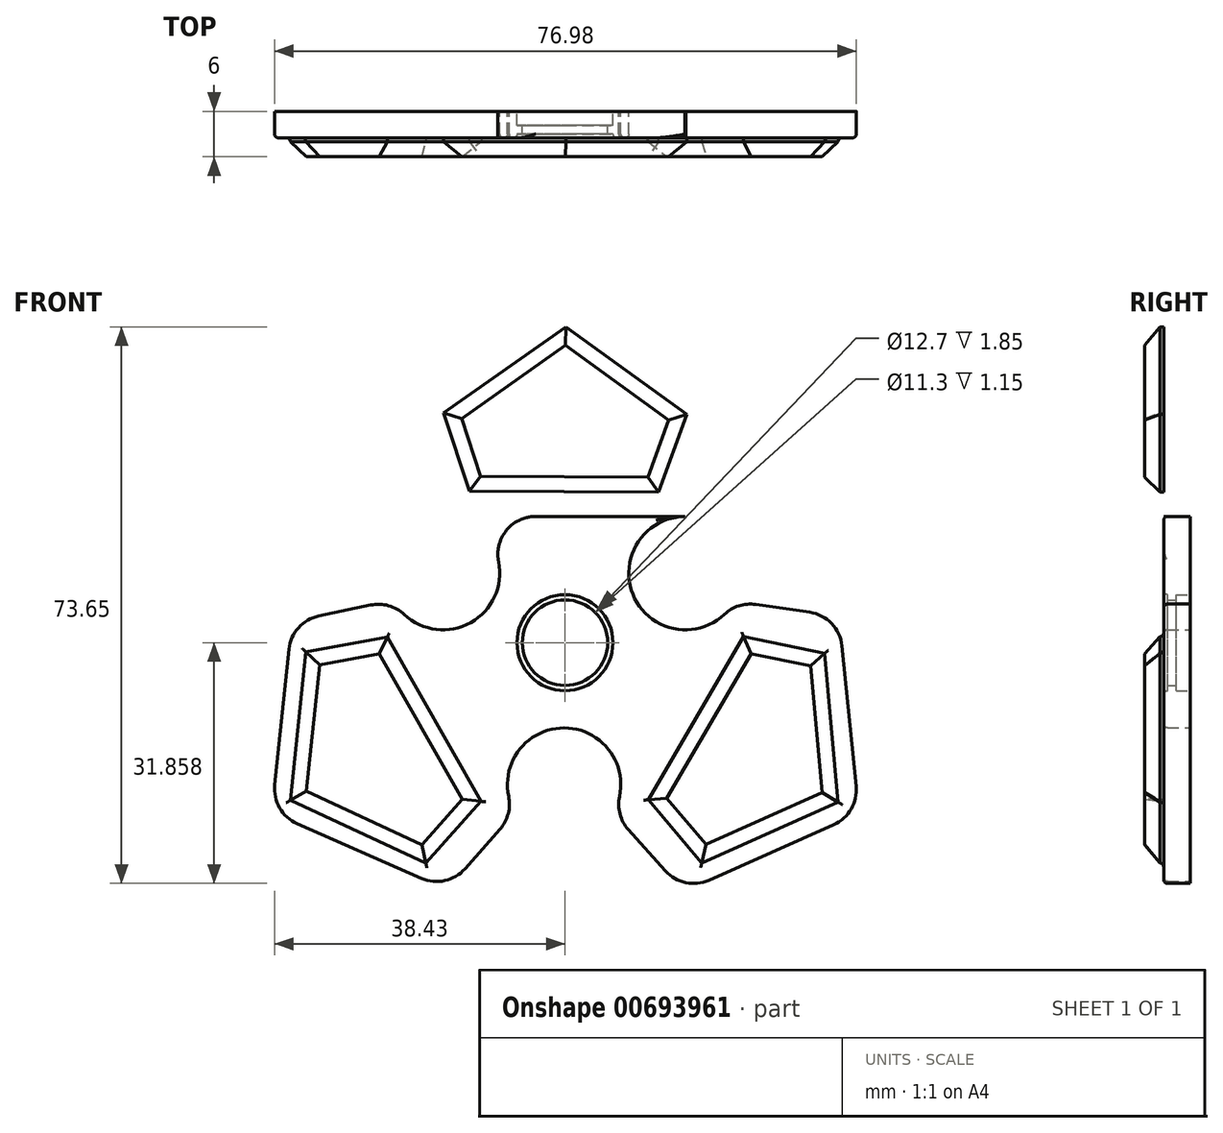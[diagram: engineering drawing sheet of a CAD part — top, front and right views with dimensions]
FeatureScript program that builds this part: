
annotation { "Feature Type Name" : "Feature", "Feature Type Description" : "" }
export const myFeature = defineFeature(function(context is Context, id is Id, definition is map)
    precondition{}
    {
        {
            var Q0;
            Q0=qCreatedBy(makeId("Front.planeOp"),FACE);
            var sketch = newSketch(context, id + "F0", { "sketchPlane" : qUnion([Q0])});
            skPoint(sketch, "E0.center", {"position": v(-0.03, -0.92) * mm});
            skLineSegment(sketch, "E1.0", {"start": v(15.99, 15.77) * mm, "end": v(-16.16, 15.77) * mm});
            skLineSegment(sketch, "E1.1", {"start": v(-16.16, 15.77) * mm, "end": v(-20.52, 29.1) * mm});
            skLineSegment(sketch, "E1.2", {"start": v(-20.52, 29.1) * mm, "end": v(0, 44.01) * mm});
            skLineSegment(sketch, "E1.3", {"start": v(0, 44.01) * mm, "end": v(20.51, 29.1) * mm});
            skLineSegment(sketch, "E1.4", {"start": v(20.51, 29.1) * mm, "end": v(15.99, 15.77) * mm});
            skPoint(sketch, "E1.0.midPoint", {"position": v(-0.09, 15.77) * mm});
            skLineSegment(sketch, "E2.1.0", {"start": v(22.42, 4.54) * mm, "end": v(36.23, 2.53) * mm});
            skLineSegment(sketch, "E2.1.2", {"start": v(36.23, 2.53) * mm, "end": v(38.86, -23.51) * mm});
            skLineSegment(sketch, "E2.1.3", {"start": v(6.36, -23.44) * mm, "end": v(22.42, 4.54) * mm});
            skLineSegment(sketch, "E2.1.4", {"start": v(15.7, -33.83) * mm, "end": v(6.36, -23.44) * mm});
            skLineSegment(sketch, "E2.1.5", {"start": v(38.86, -23.51) * mm, "end": v(15.7, -33.83) * mm});
            skLineSegment(sketch, "E2.2.0", {"start": v(-6.68, -23.39) * mm, "end": v(-15.67, -33.57) * mm});
            skLineSegment(sketch, "E2.2.2", {"start": v(-15.67, -33.57) * mm, "end": v(-38.81, -23.39) * mm});
            skLineSegment(sketch, "E2.2.3", {"start": v(-22.75, 4.69) * mm, "end": v(-6.68, -23.39) * mm});
            skLineSegment(sketch, "E2.2.4", {"start": v(-36.16, 1.84) * mm, "end": v(-22.75, 4.69) * mm});
            skLineSegment(sketch, "E2.2.5", {"start": v(-38.81, -23.39) * mm, "end": v(-36.16, 1.84) * mm});
            skPoint(sketch, "E2.center", {"position": v(0, -0.83) * mm});
            skArc(sketch, "E3", {"start": v(15.99, 15.77) * mm, "mid": v(9.4, 4.55) * mm, "end": v(22.42, 4.54) * mm});
            skArc(sketch, "E4", {"start": v(-22.75, 4.69) * mm, "mid": v(-9.71, 4.44) * mm, "end": v(-16.16, 15.77) * mm});
            skArc(sketch, "E5", {"start": v(6.36, -23.44) * mm, "mid": v(-0.11, -12.2) * mm, "end": v(-6.68, -23.39) * mm});
            skCircle(sketch, "E6", {"center": v(-0.03, -0.92) * mm, "radius": 6.35 * mm});
            skCircle(sketch, "E7", {"center": v(-0.03, -0.92) * mm, "radius": 5.65 * mm});
            skSolve(sketch);
        }
        {
            var Q0;
            Q0=makeQuery(id+"F0.imprint","IMPRINT",FACE,{"disambiguationData":[TD([[makeQuery(id+"F0.imprint","IMPRINT",EDGE,{"derivedFrom":sQuery(id+"F0.wireOp",EDGE,"E2.1.0")}),-1.0]])]});
            var Q1;
            {var subQ0=sQuery(id+"F0.wireOp",EDGE,"E1.0");Q1=makeQuery(id+"F0.imprint","IMPRINT",FACE,{"disambiguationData":[TD([[makeQuery(id+"F0.imprint","IMPRINT",EDGE,{"derivedFrom":subQ0}),-1.0]])]});}
            var Q2;
            {var subQ5=sQuery(id+"F0.wireOp",EDGE,"E1.0");Q2=makeQuery(id+"F0.imprint","IMPRINT",FACE,{"disambiguationData":[TD([[makeQuery(id+"F0.imprint","IMPRINT",EDGE,{"derivedFrom":subQ5}),1.0]])]});}
            var Q3;
            {var subQ2=sQuery(id+"F0.wireOp",EDGE,"E2.2.0");Q3=makeQuery(id+"F0.imprint","IMPRINT",FACE,{"disambiguationData":[TD([[makeQuery(id+"F0.imprint","IMPRINT",EDGE,{"derivedFrom":subQ2}),-1.0]])]});}
            extrude(context, id + "F1", {"entities" : qUnion([Q0, Q1, Q2, Q3]), "depth" : 3.5 * mm, "offsetDistance" : 25 * mm});
        }
        {
            var Q0;
            Q0=makeQuery(id+"F1.opExtrude","CAP_FACE",FACE,{"disambiguationData":[OSD([sQuery(id+"F0.wireOp",EDGE,"E1.1"),sQuery(id+"F0.wireOp",EDGE,"E1.2"),sQuery(id+"F0.wireOp",EDGE,"E1.3"),sQuery(id+"F0.wireOp",EDGE,"E1.4"),sQuery(id+"F0.wireOp",EDGE,"E2.1.0"),sQuery(id+"F0.wireOp",EDGE,"E2.1.2"),sQuery(id+"F0.wireOp",EDGE,"E2.1.4"),sQuery(id+"F0.wireOp",EDGE,"E2.1.5"),sQuery(id+"F0.wireOp",EDGE,"E2.2.0"),sQuery(id+"F0.wireOp",EDGE,"E2.2.2"),sQuery(id+"F0.wireOp",EDGE,"E2.2.4"),sQuery(id+"F0.wireOp",EDGE,"E2.2.5"),sQuery(id+"F0.wireOp",EDGE,"E3"),sQuery(id+"F0.wireOp",EDGE,"E4"),sQuery(id+"F0.wireOp",EDGE,"E5")])],"isStart":false});
            var sketch = newSketch(context, id + "F2", { "sketchPlane" : qUnion([Q0])});
            skLineSegment(sketch, "E8.0", {"start": v(12.36, 18.97) * mm, "end": v(-12.64, 19.1) * mm});
            skLineSegment(sketch, "E8.1", {"start": v(-12.64, 19.1) * mm, "end": v(-16.08, 29.5) * mm});
            skLineSegment(sketch, "E8.2", {"start": v(-16.08, 29.5) * mm, "end": v(0.08, 40.87) * mm});
            skLineSegment(sketch, "E8.3", {"start": v(0.08, 40.87) * mm, "end": v(16.07, 29.27) * mm});
            skLineSegment(sketch, "E8.4", {"start": v(16.07, 29.27) * mm, "end": v(12.36, 18.97) * mm});
            skLineSegment(sketch, "E9.1.0", {"start": v(-23.54, -0.2) * mm, "end": v(-11.15, -21.92) * mm});
            skLineSegment(sketch, "E9.1.1", {"start": v(-34.32, -2.14) * mm, "end": v(-23.54, -0.2) * mm});
            skLineSegment(sketch, "E9.1.2", {"start": v(-36.37, -21.8) * mm, "end": v(-34.32, -2.14) * mm});
            skLineSegment(sketch, "E9.1.3", {"start": v(-18.44, -30.1) * mm, "end": v(-36.37, -21.8) * mm});
            skLineSegment(sketch, "E9.1.4", {"start": v(-11.15, -21.92) * mm, "end": v(-18.44, -30.1) * mm});
            skLineSegment(sketch, "E9.2.0", {"start": v(11.01, -21.7) * mm, "end": v(23.62, -0.12) * mm});
            skLineSegment(sketch, "E9.2.1", {"start": v(18.08, -30.08) * mm, "end": v(11.01, -21.7) * mm});
            skLineSegment(sketch, "E9.2.2", {"start": v(36.12, -22.02) * mm, "end": v(18.08, -30.08) * mm});
            skLineSegment(sketch, "E9.2.3", {"start": v(34.34, -2.35) * mm, "end": v(36.12, -22.02) * mm});
            skLineSegment(sketch, "E9.2.4", {"start": v(23.62, -0.12) * mm, "end": v(34.34, -2.35) * mm});
            skPoint(sketch, "E9.center", {"position": v(-0.06, -0.98) * mm});
            skSolve(sketch);
        }
        {
            var Q0;
            Q0=makeQuery(id+"F2.imprint","IMPRINT",FACE,{"disambiguationData":[TD([[makeQuery(id+"F2.imprint","IMPRINT",EDGE,{"derivedFrom":sQuery(id+"F2.wireOp",EDGE,"E8.0")}),-1.0]])]});
            var Q1;
            Q1=makeQuery(id+"F2.imprint","IMPRINT",FACE,{"disambiguationData":[TD([[makeQuery(id+"F2.imprint","IMPRINT",EDGE,{"derivedFrom":sQuery(id+"F2.wireOp",EDGE,"E9.1.0")}),-1.0]])]});
            var Q2;
            Q2=makeQuery(id+"F2.imprint","IMPRINT",FACE,{"disambiguationData":[TD([[makeQuery(id+"F2.imprint","IMPRINT",EDGE,{"derivedFrom":sQuery(id+"F2.wireOp",EDGE,"E9.2.0")}),-1.0]])]});
            extrude(context, id + "F3", {"entities" : qUnion([Q0, Q1, Q2]), "operationType" : NewBodyOperationType.ADD, "depth" : 2.5 * mm, "offsetDistance" : 25 * mm});
        }
        {
            var Q0;
            Q0=makeQuery(id+"F3.opExtrude","CAP_FACE",FACE,{"disambiguationData":[OSD([sQuery(id+"F2.wireOp",EDGE,"E8.0"),sQuery(id+"F2.wireOp",EDGE,"E8.1"),sQuery(id+"F2.wireOp",EDGE,"E8.2"),sQuery(id+"F2.wireOp",EDGE,"E8.3"),sQuery(id+"F2.wireOp",EDGE,"E8.4")])],"isStart":false});
            var Q1;
            Q1=makeQuery(id+"F3.opExtrude","CAP_FACE",FACE,{"disambiguationData":[OSD([sQuery(id+"F2.wireOp",EDGE,"E9.2.0"),sQuery(id+"F2.wireOp",EDGE,"E9.2.1"),sQuery(id+"F2.wireOp",EDGE,"E9.2.2"),sQuery(id+"F2.wireOp",EDGE,"E9.2.3"),sQuery(id+"F2.wireOp",EDGE,"E9.2.4")])],"isStart":false});
            var Q2;
            Q2=makeQuery(id+"F3.opExtrude","CAP_FACE",FACE,{"disambiguationData":[OSD([sQuery(id+"F2.wireOp",EDGE,"E9.1.0"),sQuery(id+"F2.wireOp",EDGE,"E9.1.1"),sQuery(id+"F2.wireOp",EDGE,"E9.1.2"),sQuery(id+"F2.wireOp",EDGE,"E9.1.3"),sQuery(id+"F2.wireOp",EDGE,"E9.1.4")])],"isStart":false});
            chamfer(context, id + "F4", {"entities" : qUnion([Q0, Q1, Q2]), "width" : 2 * mm, "tangentPropagation" : true});
        }
        {
            var Q0;
            Q0=makeQuery(id+"F1.opExtrude","CAP_FACE",FACE,{"disambiguationData":[OSD([sQuery(id+"F0.wireOp",EDGE,"E1.1"),sQuery(id+"F0.wireOp",EDGE,"E1.2"),sQuery(id+"F0.wireOp",EDGE,"E1.3"),sQuery(id+"F0.wireOp",EDGE,"E1.4"),sQuery(id+"F0.wireOp",EDGE,"E2.1.0"),sQuery(id+"F0.wireOp",EDGE,"E2.1.2"),sQuery(id+"F0.wireOp",EDGE,"E2.1.4"),sQuery(id+"F0.wireOp",EDGE,"E2.1.5"),sQuery(id+"F0.wireOp",EDGE,"E2.2.0"),sQuery(id+"F0.wireOp",EDGE,"E2.2.2"),sQuery(id+"F0.wireOp",EDGE,"E2.2.4"),sQuery(id+"F0.wireOp",EDGE,"E2.2.5"),sQuery(id+"F0.wireOp",EDGE,"E3"),sQuery(id+"F0.wireOp",EDGE,"E4"),sQuery(id+"F0.wireOp",EDGE,"E5"),sQuery(id+"F0.wireOp",EDGE,"E6")])],"isStart":false});
            fillet(context, id + "F5", {"entities" : qUnion([Q0]), "radius" : 0.5 * mm, "tangentPropagation" : true, "allowEdgeOverflow" : false});
        }
        {
            var Q0;
            Q0=makeQuery(id+"F1.opExtrude","SWEPT_EDGE",EDGE,{"disambiguationData":[OSD([sQuery(id+"F0.wireOp",EDGE,"E1.0"),sQuery(id+"F0.wireOp",EDGE,"E1.1"),sQuery(id+"F0.wireOp",EDGE,"E4")])]});
            var Q1;
            Q1=makeQuery(id+"F1.opExtrude","SWEPT_EDGE",EDGE,{"disambiguationData":[OSD([sQuery(id+"F0.wireOp",EDGE,"E1.1"),sQuery(id+"F0.wireOp",EDGE,"E1.2")])]});
            var Q2;
            Q2=makeQuery(id+"F1.opExtrude","SWEPT_EDGE",EDGE,{"disambiguationData":[OSD([sQuery(id+"F0.wireOp",EDGE,"E1.2"),sQuery(id+"F0.wireOp",EDGE,"E1.3")])]});
            var Q3;
            Q3=makeQuery(id+"F1.opExtrude","SWEPT_EDGE",EDGE,{"disambiguationData":[OSD([sQuery(id+"F0.wireOp",EDGE,"E1.3"),sQuery(id+"F0.wireOp",EDGE,"E1.4")])]});
            var Q4;
            Q4=makeQuery(id+"F1.opExtrude","SWEPT_EDGE",EDGE,{"disambiguationData":[OSD([sQuery(id+"F0.wireOp",EDGE,"E1.4"),sQuery(id+"F0.wireOp",EDGE,"E3")])]});
            fillet(context, id + "F6", {"entities" : qUnion([Q0, Q1, Q2, Q3, Q4]), "radius" : 5 * mm, "tangentPropagation" : true, "allowEdgeOverflow" : false});
        }
        {
            var Q0;
            Q0=makeQuery(id+"F1.opExtrude","SWEPT_EDGE",EDGE,{"disambiguationData":[OSD([sQuery(id+"F0.wireOp",EDGE,"E2.1.4"),sQuery(id+"F0.wireOp",EDGE,"E2.1.5")])]});
            var Q1;
            Q1=makeQuery(id+"F1.opExtrude","SWEPT_EDGE",EDGE,{"disambiguationData":[OSD([sQuery(id+"F0.wireOp",EDGE,"E2.1.3"),sQuery(id+"F0.wireOp",EDGE,"E2.1.4"),sQuery(id+"F0.wireOp",EDGE,"E5")])]});
            var Q2;
            Q2=makeQuery(id+"F1.opExtrude","SWEPT_EDGE",EDGE,{"disambiguationData":[OSD([sQuery(id+"F0.wireOp",EDGE,"E2.1.2"),sQuery(id+"F0.wireOp",EDGE,"E2.1.5")])]});
            var Q3;
            Q3=makeQuery(id+"F1.opExtrude","SWEPT_EDGE",EDGE,{"disambiguationData":[OSD([sQuery(id+"F0.wireOp",EDGE,"E2.1.0"),sQuery(id+"F0.wireOp",EDGE,"E2.1.2")])]});
            var Q4;
            Q4=makeQuery(id+"F1.opExtrude","SWEPT_EDGE",EDGE,{"disambiguationData":[OSD([sQuery(id+"F0.wireOp",EDGE,"E2.1.0"),sQuery(id+"F0.wireOp",EDGE,"E2.1.3"),sQuery(id+"F0.wireOp",EDGE,"E3")])]});
            fillet(context, id + "F7", {"entities" : qUnion([Q0, Q1, Q2, Q3, Q4]), "radius" : 5 * mm, "tangentPropagation" : true, "allowEdgeOverflow" : false});
        }
        {
            var Q0;
            Q0=makeQuery(id+"F1.opExtrude","SWEPT_EDGE",EDGE,{"disambiguationData":[OSD([sQuery(id+"F0.wireOp",EDGE,"E2.2.0"),sQuery(id+"F0.wireOp",EDGE,"E2.2.2")])]});
            var Q1;
            Q1=makeQuery(id+"F1.opExtrude","SWEPT_EDGE",EDGE,{"disambiguationData":[OSD([sQuery(id+"F0.wireOp",EDGE,"E2.2.0"),sQuery(id+"F0.wireOp",EDGE,"E2.2.3"),sQuery(id+"F0.wireOp",EDGE,"E5")])]});
            var Q2;
            Q2=makeQuery(id+"F1.opExtrude","SWEPT_EDGE",EDGE,{"disambiguationData":[OSD([sQuery(id+"F0.wireOp",EDGE,"E2.2.2"),sQuery(id+"F0.wireOp",EDGE,"E2.2.5")])]});
            var Q3;
            Q3=makeQuery(id+"F1.opExtrude","SWEPT_EDGE",EDGE,{"disambiguationData":[OSD([sQuery(id+"F0.wireOp",EDGE,"E2.2.4"),sQuery(id+"F0.wireOp",EDGE,"E2.2.5")])]});
            var Q4;
            Q4=makeQuery(id+"F1.opExtrude","SWEPT_EDGE",EDGE,{"disambiguationData":[OSD([sQuery(id+"F0.wireOp",EDGE,"E2.2.3"),sQuery(id+"F0.wireOp",EDGE,"E2.2.4"),sQuery(id+"F0.wireOp",EDGE,"E4")])]});
            fillet(context, id + "F8", {"entities" : qUnion([Q0, Q1, Q2, Q3, Q4]), "radius" : 5 * mm, "tangentPropagation" : true, "allowEdgeOverflow" : false});
        }
        {
            var Q0;
            Q0=makeQuery(id+"F0.imprint","IMPRINT",FACE,{"disambiguationData":[TD([[makeQuery(id+"F0.imprint","IMPRINT",EDGE,{"derivedFrom":sQuery(id+"F0.wireOp",EDGE,"E6")}),1.0]])]});
            extrude(context, id + "F9", {"entities" : qUnion([Q0]), "operationType" : NewBodyOperationType.ADD, "depth" : 3 * mm, "offsetDistance" : 25 * mm, "hasSecondDirection" : true, "secondDirectionOppositeDirection" : false, "secondDirectionDepth" : 1.85 * mm});
        }
    });
